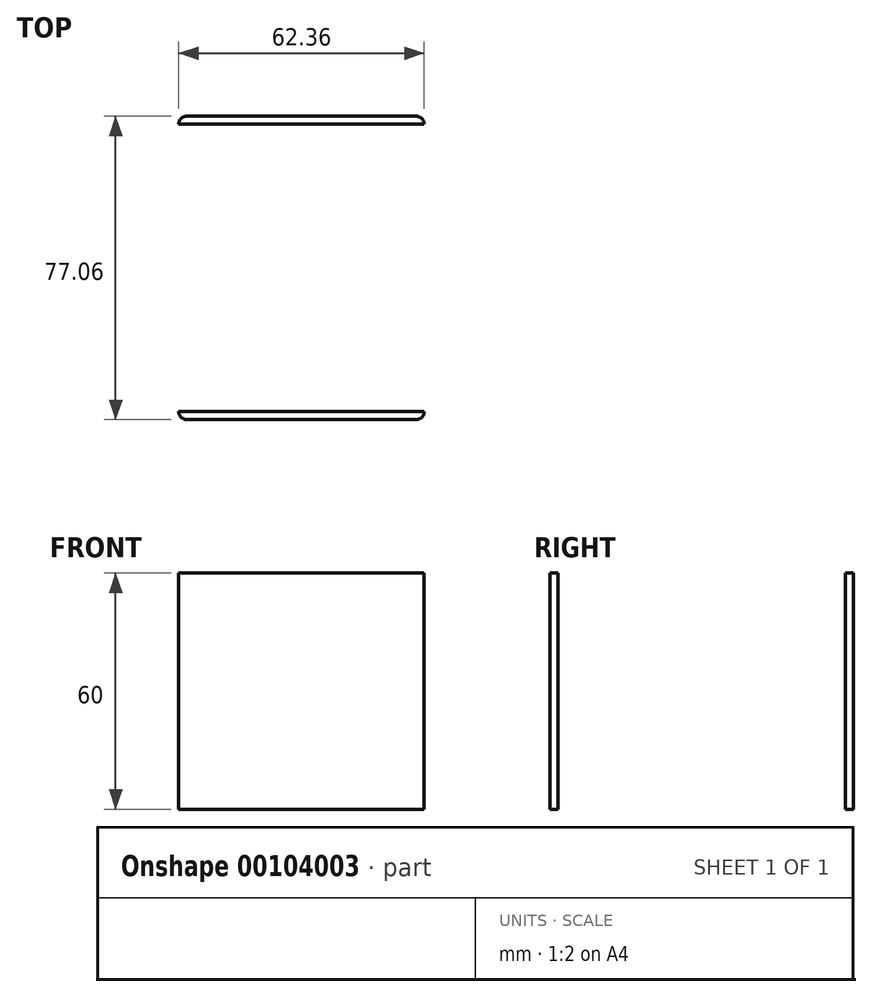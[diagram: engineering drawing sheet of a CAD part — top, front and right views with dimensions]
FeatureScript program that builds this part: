
annotation { "Feature Type Name" : "Feature", "Feature Type Description" : "" }
export const myFeature = defineFeature(function(context is Context, id is Id, definition is map)
    precondition{}
    {
        {
            var Q0;
            Q0=qCreatedBy(makeId("Top.planeOp"),FACE);
            var sketch = newSketch(context, id + "F0", { "sketchPlane" : qUnion([Q0])});
            skLineSegment(sketch, "E0.bottom", {"start": v(31.18, -38.53) * mm, "end": v(-31.18, -38.53) * mm});
            skLineSegment(sketch, "E0.top", {"start": v(31.18, 38.53) * mm, "end": v(-31.18, 38.53) * mm});
            skLineSegment(sketch, "E0.left", {"start": v(31.18, -38.53) * mm, "end": v(31.18, 38.53) * mm});
            skLineSegment(sketch, "E0.right", {"start": v(-31.18, -38.53) * mm, "end": v(-31.18, 38.53) * mm});
            skPoint(sketch, "E0.middle", {"position": v(0, 0) * mm});
            skLineSegment(sketch, "E1.bottom", {"start": v(19.7, -25.89) * mm, "end": v(-19.7, -25.89) * mm});
            skLineSegment(sketch, "E1.top", {"start": v(19.7, 25.89) * mm, "end": v(-19.7, 25.89) * mm});
            skLineSegment(sketch, "E1.left", {"start": v(19.7, -25.89) * mm, "end": v(19.7, 25.89) * mm});
            skLineSegment(sketch, "E1.right", {"start": v(-19.7, -25.89) * mm, "end": v(-19.7, 25.89) * mm});
            skSolve(sketch);
        }
        {
            var Q0;
            Q0=makeQuery(id+"F0.imprint","IMPRINT",FACE,{"disambiguationData":[TD([[makeQuery(id+"F0.imprint","IMPRINT",EDGE,{"derivedFrom":sQuery(id+"F0.wireOp",EDGE,"E0.bottom")}),-1.0]])]});
            extrude(context, id + "F1", {"entities" : qUnion([Q0]), "depth" : 60 * mm});
        }
        {
            var Q0;
            Q0=makeQuery(id+"F1.opExtrude","SWEPT_EDGE",EDGE,{"disambiguationData":[OSD([sQuery(id+"F0.wireOp",EDGE,"E0.top"),sQuery(id+"F0.wireOp",EDGE,"E0.right")])]});
            var Q1;
            Q1=makeQuery(id+"F1.opExtrude","SWEPT_EDGE",EDGE,{"disambiguationData":[OSD([sQuery(id+"F0.wireOp",EDGE,"E0.bottom"),sQuery(id+"F0.wireOp",EDGE,"E0.right")])]});
            var Q2;
            Q2=makeQuery(id+"F1.opExtrude","SWEPT_EDGE",EDGE,{"disambiguationData":[OSD([sQuery(id+"F0.wireOp",EDGE,"E0.bottom"),sQuery(id+"F0.wireOp",EDGE,"E0.left")])]});
            var Q3;
            Q3=makeQuery(id+"F1.opExtrude","SWEPT_EDGE",EDGE,{"disambiguationData":[OSD([sQuery(id+"F0.wireOp",EDGE,"E0.top"),sQuery(id+"F0.wireOp",EDGE,"E0.left")])]});
            fillet(context, id + "F2", {"entities" : qUnion([Q0, Q1, Q2, Q3]), "radius" : 2 * mm, "tangentPropagation" : true, "allowEdgeOverflow" : false});
        }
        {
            var Q0;
            Q0=makeQuery(id+"F1.opExtrude","SWEPT_FACE",FACE,{"disambiguationData":[OSD([sQuery(id+"F0.wireOp",EDGE,"E0.left")])]});
            extrude(context, id + "F3", {"entities" : qUnion([Q0]), "operationType" : NewBodyOperationType.REMOVE, "oppositeDirection" : true, "depth" : 70 * mm});
        }
    });
